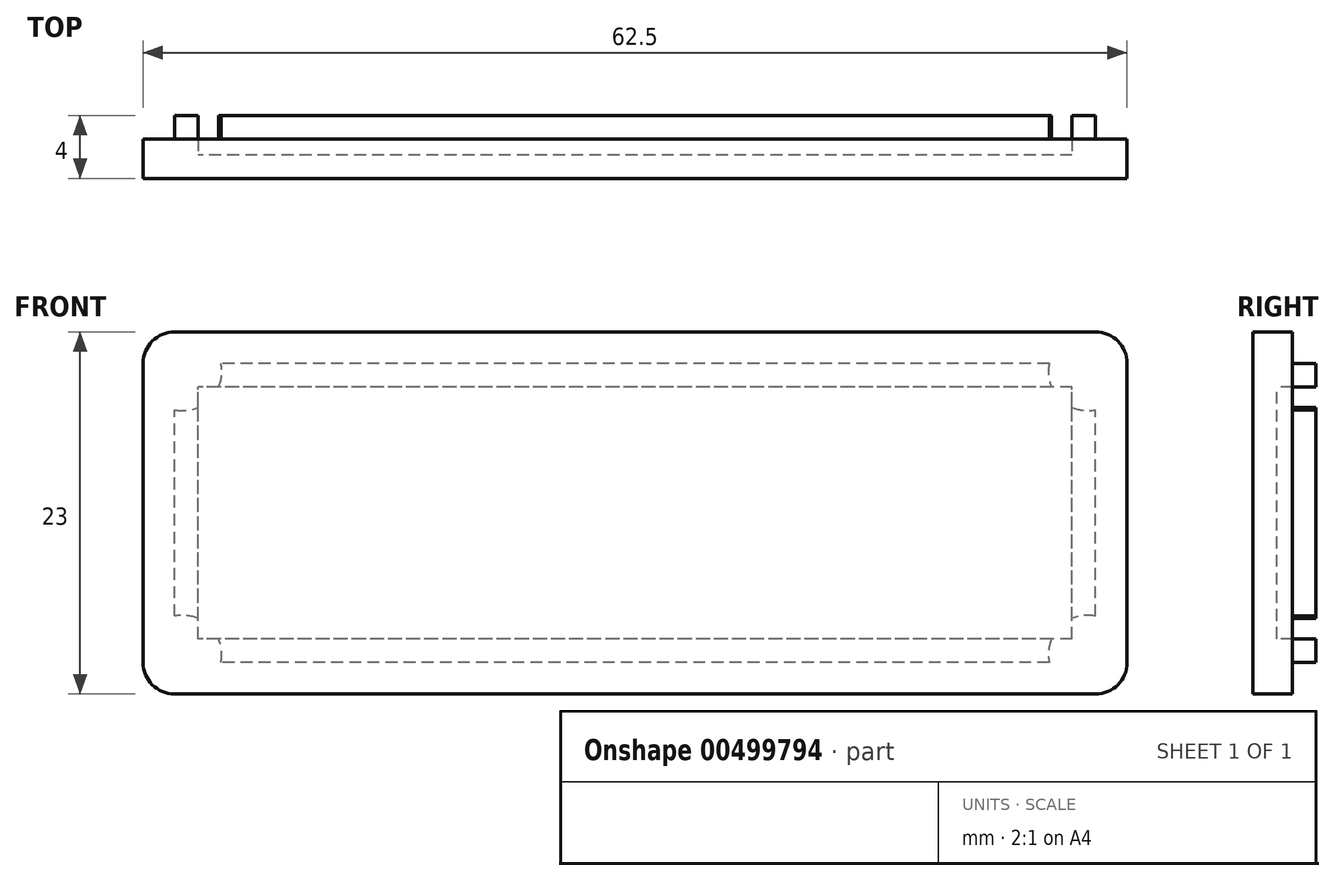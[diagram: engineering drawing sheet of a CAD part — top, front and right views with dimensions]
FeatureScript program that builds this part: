
annotation { "Feature Type Name" : "Feature", "Feature Type Description" : "" }
export const myFeature = defineFeature(function(context is Context, id is Id, definition is map)
    precondition{}
    {
        {
            var Q0;
            Q0=qCreatedBy(makeId("Front.planeOp"),FACE);
            var sketch = newSketch(context, id + "F0", { "sketchPlane" : qUnion([Q0])});
            skLineSegment(sketch, "E0.bottom", {"start": v(31.25, -11.5) * mm, "end": v(-31.25, -11.5) * mm});
            skLineSegment(sketch, "E0.top", {"start": v(31.25, 11.5) * mm, "end": v(-31.25, 11.5) * mm});
            skLineSegment(sketch, "E0.left", {"start": v(31.25, -11.5) * mm, "end": v(31.25, 11.5) * mm});
            skLineSegment(sketch, "E0.right", {"start": v(-31.25, -11.5) * mm, "end": v(-31.25, 11.5) * mm});
            skPoint(sketch, "E0.middle", {"position": v(0, 0) * mm});
            skSolve(sketch);
        }
        {
            var Q0;
            Q0=makeQuery(id+"F0.imprint","IMPRINT",FACE,{"disambiguationData":[TD([[makeQuery(id+"F0.imprint","IMPRINT",EDGE,{"derivedFrom":sQuery(id+"F0.wireOp",EDGE,"E0.bottom")}),-1.0]])]});
            var Q1;
            Q1 = qSketchRegion(id + "FelRyDtBHo83BtA_1", true);
            extrude(context, id + "F1", {"entities" : qUnion([Q0, Q1]), "depth" : 2.5 * mm});
        }
        {
            var Q0;
            Q0=makeQuery(id+"F1.opExtrude","CAP_FACE",FACE,{"disambiguationData":[OSD([sQuery(id+"F0.wireOp",EDGE,"E0.bottom"),sQuery(id+"F0.wireOp",EDGE,"E0.top"),sQuery(id+"F0.wireOp",EDGE,"E0.left"),sQuery(id+"F0.wireOp",EDGE,"E0.right")])],"isStart":true});
            shell(context, id + "F2", {"entities" : qUnion([Q0]), "thickness" : 2 * mm});
        }
        {
            var Q0;
            Q0=makeQuery(id+"F1.opExtrude","SWEPT_EDGE",EDGE,{"disambiguationData":[OSD([sQuery(id+"F0.wireOp",EDGE,"E0.top"),sQuery(id+"F0.wireOp",EDGE,"E0.right")])]});
            var Q1;
            Q1=makeQuery(id+"F1.opExtrude","SWEPT_EDGE",EDGE,{"disambiguationData":[OSD([sQuery(id+"F0.wireOp",EDGE,"E0.bottom"),sQuery(id+"F0.wireOp",EDGE,"E0.right")])]});
            var Q2;
            Q2=makeQuery(id+"F1.opExtrude","SWEPT_EDGE",EDGE,{"disambiguationData":[OSD([sQuery(id+"F0.wireOp",EDGE,"E0.top"),sQuery(id+"F0.wireOp",EDGE,"E0.left")])]});
            var Q3;
            Q3=makeQuery(id+"F1.opExtrude","SWEPT_EDGE",EDGE,{"disambiguationData":[OSD([sQuery(id+"F0.wireOp",EDGE,"E0.bottom"),sQuery(id+"F0.wireOp",EDGE,"E0.left")])]});
            fillet(context, id + "F3", {"entities" : qUnion([Q0, Q1, Q2, Q3]), "radius" : 2 * mm, "tangentPropagation" : true, "allowEdgeOverflow" : false});
        }
        {
            var Q0;
            {var subQ0=sQuery(id+"F0.wireOp",EDGE,"E0.right");var subQ1=sQuery(id+"F0.wireOp",EDGE,"E0.left");var subQ2=sQuery(id+"F0.wireOp",EDGE,"E0.top");var subQ3=sQuery(id+"F0.wireOp",EDGE,"E0.bottom");Q0=makeQuery(id+"F8vEHVh69V0LH0B_5.boolean.opBoolean","SPLIT",FACE,{"disambiguationData":[TD([makeQuery(id+"F2.opShell","OFFSET_FACE",FACE,{"disambiguationData":[OSD([subQ3])]})])],"derivedFrom":makeQuery(id+"F2.opShell","OFFSET_FACE",FACE,{"disambiguationData":[OSD([subQ3,subQ2,subQ1,subQ0])]})});}
            extrude(context, id + "F4", {"entities" : qUnion([Q0]), "operationType" : NewBodyOperationType.ADD, "depth" : 2 * mm, "offsetDistance" : 25 * mm});
        }
        {
            var Q0;
            Q0=makeQuery(id+"F4.opExtrude","CAP_FACE",FACE,{"disambiguationData":[OSD([sQuery(id+"F0.wireOp",EDGE,"E0.bottom"),sQuery(id+"F0.wireOp",EDGE,"E0.top"),sQuery(id+"F0.wireOp",EDGE,"E0.left"),sQuery(id+"F0.wireOp",EDGE,"E0.right")])],"isStart":false});
            shell(context, id + "F5", {"entities" : qUnion([Q0]), "thickness" : 1.5 * mm});
        }
        {
            var Q0;
            Q0=makeQuery(id+"F1.opExtrude","CAP_FACE",FACE,{"disambiguationData":[OSD([sQuery(id+"F0.wireOp",EDGE,"E0.bottom"),sQuery(id+"F0.wireOp",EDGE,"E0.top"),sQuery(id+"F0.wireOp",EDGE,"E0.left"),sQuery(id+"F0.wireOp",EDGE,"E0.right")])],"isStart":true});
            var sketch = newSketch(context, id + "F6", { "sketchPlane" : qUnion([Q0])});
            skPoint(sketch, "E1", {"position": v(-28.75, 9) * mm});
            skCircle(sketch, "E2", {"center": v(-28.75, 9) * mm, "radius": 2.5 * mm});
            skCircle(sketch, "E3.MirrorC", {"center": v(28.75, 9) * mm, "radius": 2.5 * mm});
            skCircle(sketch, "E4.MirrorC", {"center": v(28.75, -9) * mm, "radius": 2.5 * mm});
            skCircle(sketch, "E5.MirrorC", {"center": v(-28.75, -9) * mm, "radius": 2.5 * mm});
            skSolve(sketch);
        }
        {
            var Q0;
            Q0 = qSketchRegion(id + "F6", true);
            extrude(context, id + "F7", {"entities" : qUnion([Q0]), "operationType" : NewBodyOperationType.REMOVE, "depth" : 2 * mm, "offsetDistance" : 25 * mm});
        }
    });
